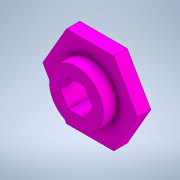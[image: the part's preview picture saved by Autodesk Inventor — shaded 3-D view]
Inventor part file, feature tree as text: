
AUTODESK INVENTOR PART (.ipt)
format: ipt  version: 2021.2 (Build 252289000, 289)  size: 141,824 bytes
history: native  units: in
note: dims shown in document units (in); Inventor stores cm internally (conversion verified against a paired STEP export)
features: extrude x2, other x2, sketch x1
ambient origin geometry x8: Origin, YZ Plane, XZ Plane, XY Plane, X Axis, Y Axis, Z Axis, Center Point
bodies: Solid1 (feature_tree)
feature tree (5):
  extrude  "Extrusion1"  Depth=1.0in
  extrude  "Extrusion3"  Depth=0.25in
  other  "Thicken Internal Hex Hold"
  other  "Reduce Size of Bushing Fitting"
  sketch  "Sketch1"  dims[d0=0.5in d2=1.0in d3=0.2113in d4=0.25in d5=0.0in d7=0.5in d10=1.5in d11=0.25in d12=0.0in d13=0.005in d14=0.005in d15=0.005in d16=0.005in]
